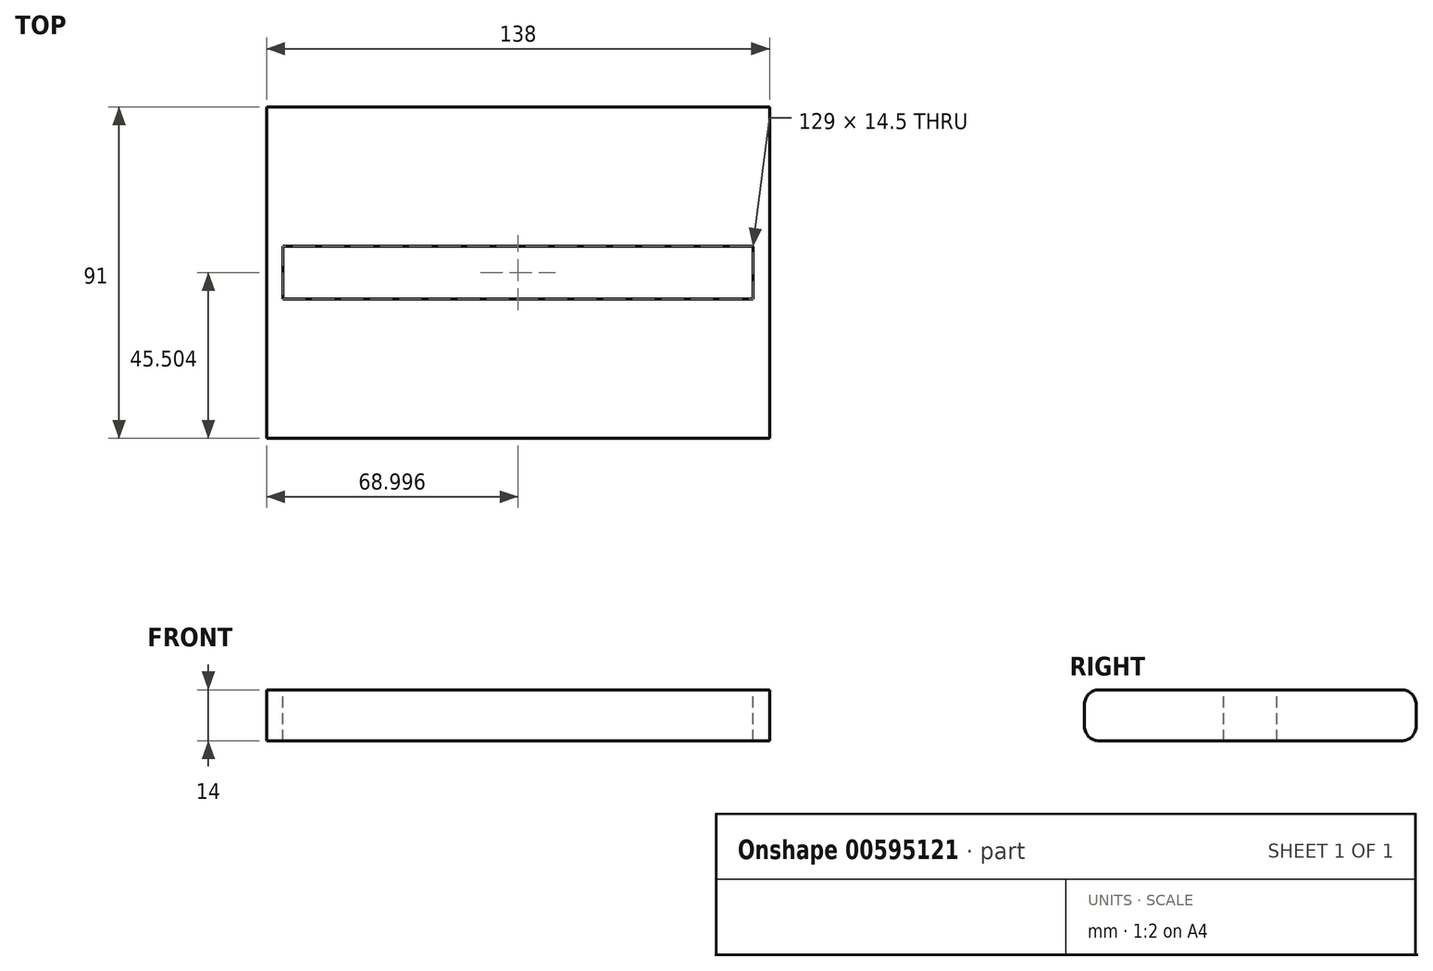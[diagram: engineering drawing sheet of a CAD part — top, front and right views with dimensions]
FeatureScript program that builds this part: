
annotation { "Feature Type Name" : "Feature", "Feature Type Description" : "" }
export const myFeature = defineFeature(function(context is Context, id is Id, definition is map)
    precondition{}
    {
        {
            var Q0;
            Q0=qCreatedBy(makeId("Top.planeOp"),FACE);
            var sketch = newSketch(context, id + "F0", { "sketchPlane" : qUnion([Q0])});
            skLineSegment(sketch, "E0.bottom", {"start": v(-23.56, -25.04) * mm, "end": v(114.44, -25.04) * mm});
            skLineSegment(sketch, "E0.top", {"start": v(-23.56, 65.96) * mm, "end": v(114.44, 65.96) * mm});
            skLineSegment(sketch, "E0.left", {"start": v(-23.56, -25.04) * mm, "end": v(-23.56, 65.96) * mm});
            skLineSegment(sketch, "E0.right", {"start": v(114.44, -25.04) * mm, "end": v(114.44, 65.96) * mm});
            skSolve(sketch);
        }
        {
            var Q0;
            Q0 = qSketchRegion(id + "F0", true);
            extrude(context, id + "F1", {"entities" : qUnion([Q0]), "depth" : 14 * mm, "offsetDistance" : 25.4 * mm});
        }
        {
            var Q0;
            Q0=makeQuery(id+"F1.opExtrude","CAP_FACE",FACE,{"disambiguationData":[OSD([sQuery(id+"F0.wireOp",EDGE,"E0.bottom"),sQuery(id+"F0.wireOp",EDGE,"E0.top"),sQuery(id+"F0.wireOp",EDGE,"E0.left"),sQuery(id+"F0.wireOp",EDGE,"E0.right")])],"isStart":false});
            var sketch = newSketch(context, id + "F2", { "sketchPlane" : qUnion([Q0])});
            skLineSegment(sketch, "E1.bottom", {"start": v(-19.06, 27.71) * mm, "end": v(109.94, 27.71) * mm});
            skLineSegment(sketch, "E1.top", {"start": v(-19.06, 13.21) * mm, "end": v(109.94, 13.21) * mm});
            skLineSegment(sketch, "E1.left", {"start": v(-19.06, 27.71) * mm, "end": v(-19.06, 13.21) * mm});
            skLineSegment(sketch, "E1.right", {"start": v(109.94, 27.71) * mm, "end": v(109.94, 13.21) * mm});
            skSolve(sketch);
        }
        {
            var Q0;
            Q0 = qSketchRegion(id + "F2", true);
            extrude(context, id + "F3", {"entities" : qUnion([Q0]), "operationType" : NewBodyOperationType.REMOVE, "oppositeDirection" : true, "depth" : 25.4 * mm, "offsetDistance" : 25.4 * mm});
        }
        {
            var Q0;
            Q0=makeQuery(id+"F1.opExtrude","CAP_EDGE",EDGE,{"disambiguationData":[OSD([sQuery(id+"F0.wireOp",EDGE,"E0.top")])],"isStart":false});
            var Q1;
            Q1=makeQuery(id+"F1.opExtrude","CAP_EDGE",EDGE,{"disambiguationData":[OSD([sQuery(id+"F0.wireOp",EDGE,"E0.bottom")])],"isStart":true});
            var Q2;
            Q2=makeQuery(id+"F1.opExtrude","CAP_EDGE",EDGE,{"disambiguationData":[OSD([sQuery(id+"F0.wireOp",EDGE,"E0.bottom")])],"isStart":false});
            var Q3;
            Q3=makeQuery(id+"F1.opExtrude","CAP_EDGE",EDGE,{"disambiguationData":[OSD([sQuery(id+"F0.wireOp",EDGE,"E0.top")])],"isStart":true});
            fillet(context, id + "F4", {"entities" : qUnion([Q0, Q1, Q2, Q3]), "radius" : 4 * mm, "tangentPropagation" : true, "allowEdgeOverflow" : false});
        }
    });
